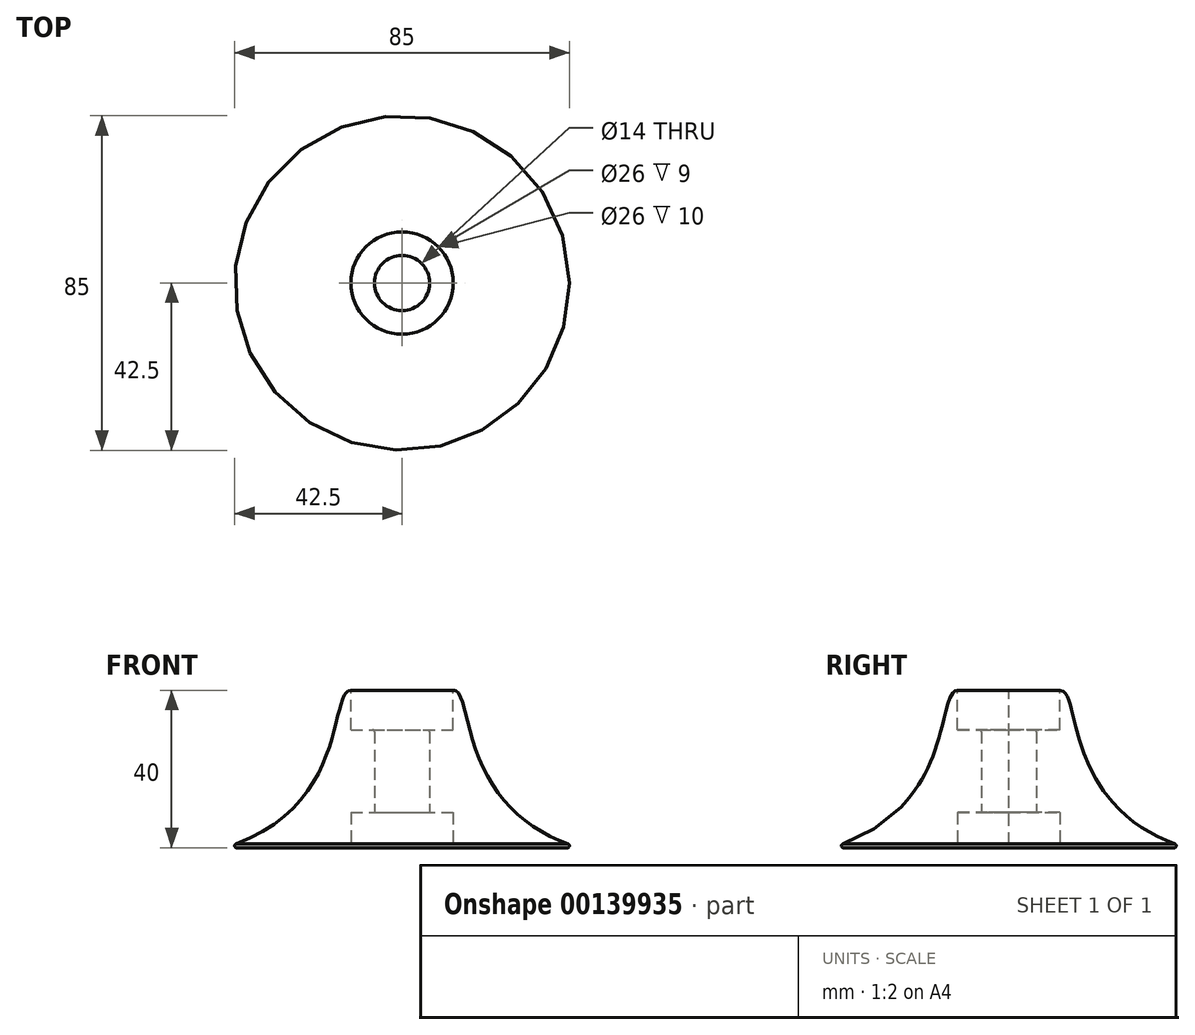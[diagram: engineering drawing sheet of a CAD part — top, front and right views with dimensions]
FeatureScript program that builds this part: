
annotation { "Feature Type Name" : "Feature", "Feature Type Description" : "" }
export const myFeature = defineFeature(function(context is Context, id is Id, definition is map)
    precondition{}
    {
        {
            var Q0;
            Q0=qCreatedBy(makeId("Front.planeOp"),FACE);
            var sketch = newSketch(context, id + "F0", { "sketchPlane" : qUnion([Q0])});
            skLineSegment(sketch, "E0", {"start": v(0, 0) * mm, "end": v(-45, 0) * mm});
            skLineSegment(sketch, "E1", {"start": v(-13, 40) * mm, "end": v(0, 40) * mm});
            skLineSegment(sketch, "E2", {"start": v(0, 40) * mm, "end": v(0, 0) * mm});
            skFitSpline(sketch, "E3", {"points": [v(-45, 0) * mm, v(-13, 40) * mm], "startDerivative": vector(96, 30) * mm, "endDerivative": vector(17.1, -0.13) * mm});
            skLineSegment(sketch, "E4", {"start": v(-16, 50.33) * mm, "end": v(-16, 0) * mm, "construction": true});
            skSolve(sketch);
        }
        {
            var Q0;
            Q0=makeQuery(id+"F0.imprint","IMPRINT",FACE,{"disambiguationData":[TD([[makeQuery(id+"F0.imprint","IMPRINT",EDGE,{"derivedFrom":sQuery(id+"F0.wireOp",EDGE,"E0")}),-1.0]])]});
            var Q1;
            Q1=sQuery(id+"F0.wireOp",EDGE,"E2");
            revolve(context, id + "F1", {"entities" : qUnion([Q0]), "axis" : qUnion([Q1]), "revolveType" : RevolveType.FULL});
        }
        {
            var Q0;
            Q0=makeQuery(id+"F1.opRevolve","SWEPT_FACE",FACE,{"disambiguationData":[OSD([sQuery(id+"F0.wireOp",EDGE,"E0")])]});
            var sketch = newSketch(context, id + "F2", { "sketchPlane" : qUnion([Q0])});
            skCircle(sketch, "E5", {"center": v(0, 0) * mm, "radius": 13 * mm});
            skCircle(sketch, "E6", {"center": v(0, 0) * mm, "radius": 7 * mm});
            skSolve(sketch);
        }
        {
            var Q0;
            Q0=makeQuery(id+"F2.imprint","IMPRINT",FACE,{"disambiguationData":[TD([[makeQuery(id+"F2.imprint","IMPRINT",EDGE,{"derivedFrom":sQuery(id+"F2.wireOp",EDGE,"E6")}),1.0]])]});
            extrude(context, id + "F3", {"entities" : qUnion([Q0]), "operationType" : NewBodyOperationType.REMOVE, "oppositeDirection" : true, "depth" : 50 * mm});
        }
        {
            var Q0;
            Q0=makeQuery(id+"F2.imprint","IMPRINT",FACE,{"disambiguationData":[TD([[makeQuery(id+"F2.imprint","IMPRINT",EDGE,{"derivedFrom":sQuery(id+"F2.wireOp",EDGE,"E5")}),1.0]])]});
            extrude(context, id + "F4", {"entities" : qUnion([Q0]), "operationType" : NewBodyOperationType.REMOVE, "oppositeDirection" : true, "depth" : 9 * mm});
        }
        {
            var Q0;
            Q0=sQuery(id+"F0.wireOp",VERTEX,"E2.start");
            var Q1;
            Q1=sQuery(id+"F0.wireOp",EDGE,"E2");
            cPlane(context, id + "F5", {"entities" : qUnion([Q0, Q1]), "cplaneType" : CPlaneType.LINE_POINT, "offset" : 25 * mm, "width" : 150 * mm, "height" : 150 * mm});
        }
        {
            var Q0;
            Q0=qCreatedBy(id+"F5.planeOp",FACE);
            var sketch = newSketch(context, id + "F6", { "sketchPlane" : qUnion([Q0])});
            skCircle(sketch, "E7", {"center": v(0, 0) * mm, "radius": 13 * mm});
            skSolve(sketch);
        }
        {
            var Q0;
            Q0=makeQuery(id+"F6.imprint","IMPRINT",FACE,{"disambiguationData":[TD([[makeQuery(id+"F6.imprint","IMPRINT",EDGE,{"derivedFrom":sQuery(id+"F6.wireOp",EDGE,"E7")}),1.0]])]});
            var Q1;
            Q1=sQuery(id+"F6.wireOp",EDGE,"E7");
            extrude(context, id + "F7", {"entities" : qUnion([Q0]), "operationType" : NewBodyOperationType.REMOVE, "surfaceEntities" : qUnion([Q1]), "depth" : 10 * mm});
        }
        {
            var Q0;
            Q0=makeQuery(id+"F7.boolean.opBoolean","INTERSECT",EDGE,{"derivedFrom":[makeQuery(id+"F3.boolean.opBoolean","COPY",FACE,{"derivedFrom":makeQuery(id+"F3.opExtrude","SWEPT_FACE",FACE,{"disambiguationData":[OSD([sQuery(id+"F2.wireOp",EDGE,"E6")])]})}),makeQuery(id+"F7.opExtrude","CAP_FACE",FACE,{"disambiguationData":[OSD([sQuery(id+"F6.wireOp",EDGE,"E7")])],"isStart":false})]});
            var Q1;
            Q1=makeQuery(id+"F4.boolean.opBoolean","COPY",EDGE,{"derivedFrom":makeQuery(id+"F4.opExtrude","CAP_EDGE",EDGE,{"disambiguationData":[OSD([sQuery(id+"F2.wireOp",EDGE,"E6")])],"isStart":false})});
            var Q2;
            Q2=makeQuery(id+"F1.opRevolve","SWEPT_EDGE",EDGE,{"disambiguationData":[OSD([sQuery(id+"F0.wireOp",EDGE,"528b37c9-0628-4f0b-8909-75498eed1815"),sQuery(id+"F0.wireOp",EDGE,"E0")])]});
            fillet(context, id + "F8", {"entities" : qUnion([Q0, Q1, Q2]), "radius" : 0.5 * mm, "tangentPropagation" : true, "allowEdgeOverflow" : false});
        }
    });
